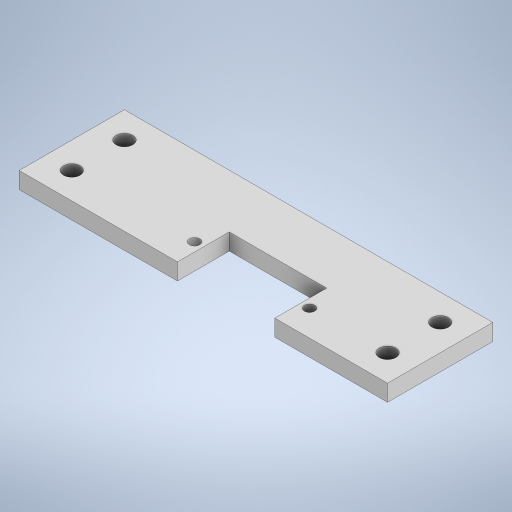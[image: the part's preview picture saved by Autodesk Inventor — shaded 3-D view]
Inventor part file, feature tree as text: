
AUTODESK INVENTOR PART (.ipt)
format: ipt  version: 2023.1 (Build 271208000, 208)  size: 579,072 bytes
history: native  units: mm
features: extrude x1, sketch x1
ambient origin geometry x8: Origin, YZ Plane, XZ Plane, XY Plane, X Axis, Y Axis, Z Axis, Center Point
bodies: Solid1 (feature_tree)
feature tree (2):
  extrude  "Extrusion1"  Depth=4.0mm
  sketch  "Sketch1"  dims[d0=25.4mm d1=76.2mm d2=12.7mm d3=88.9mm d4=6.35mm d5=6.35mm d6=4.0mm d7=4.0mm d8=4.0mm d9=4.0mm d11=32.0mm d12=23.5mm d13=12.5mm d14=2.5mm d15=2.5mm d16=23.0mm d17=6.0mm d18=4.0mm d19=0.0mm d20=0.0mm d21=0.0mm d22=0.0mm d23=0.0mm]
